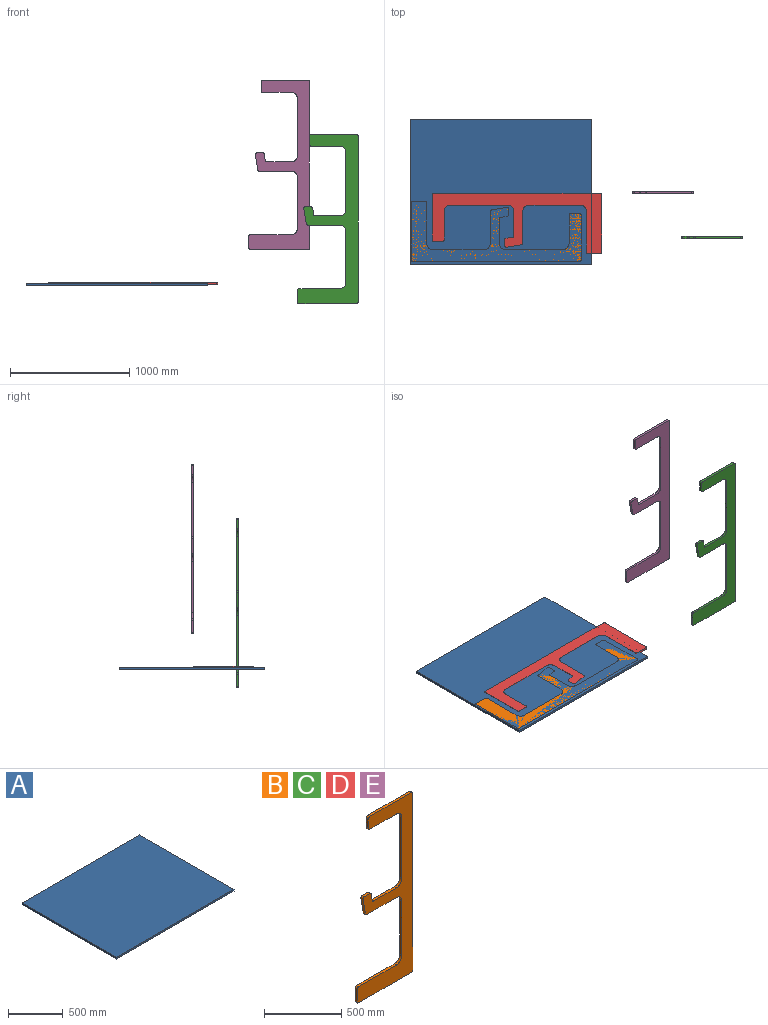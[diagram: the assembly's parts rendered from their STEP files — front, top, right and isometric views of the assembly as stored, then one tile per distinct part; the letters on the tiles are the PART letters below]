
ASSEMBLY  parts=5 mates=1
PART A: 6 faces, bbox 1524x1219.2x19.1 mm
  f0: plane 1524x19.05mm, normal (0,1,0), area 29032.2mm2, adj f1,f3,f4,f5
  f1: plane 1219.2x19.05mm, normal (-1,0,0), area 23225.8mm2, adj f0,f2,f4,f5
  f2: plane 1524x19.05mm, normal (0,-1,0), area 29032.2mm2, adj f1,f3,f4,f5
  f3: plane 1219.2x19.05mm, normal (1,0,0), area 23225.8mm2, adj f0,f2,f4,f5
  f4: plane 1524x1219.2mm, normal (0,0,1), area 1858060.8mm2, adj f0,f1,f2,f3
  f5: plane 1524x1219.2mm, normal (0,0,-1), area 1858060.8mm2, adj f0,f1,f2,f3
PART B: 30 faces, bbox 508x19.1x1422.4 mm
  f0: plane 54.98x19.05mm, normal (0.99,0,0.16), area 1061.7mm2, adj f1,f27,f28,f29
  f1: cylinder r=12.7mm len=19.05mm, axis (0,1,0), area 340.1mm2, adj f0,f2,f28,f29
  f2: plane 50.45x19.05mm, normal (0,0,1), area 961.1mm2, adj f1,f3,f28,f29
  f3: cylinder r=12.7mm len=19.05mm, axis (0,1,0), area 420mm2, adj f2,f4,f28,f29
  f4: plane 127x21.17mm, normal (-0.99,0,-0.16), area 2452.7mm2, adj f3,f5,f28,f29
  f5: cylinder r=12.7mm len=19.05mm, axis (0,1,0), area 340.1mm2, adj f4,f6,f28,f29
  f6: plane 268.64x19.05mm, normal (0,0,-1), area 5117.6mm2, adj f5,f7,f28,f29
  f7: cylinder r=50.8mm len=50.8mm, axis (0,1,0), area 1520.1mm2, adj f6,f8,f28,f29
  f8: plane 431.8x19.05mm, normal (-1,0,0), area 8225.8mm2, adj f7,f9,f28,f29
  f9: cylinder r=50.8mm len=50.8mm, axis (0,1,0), area 1520.1mm2, adj f8,f10,f28,f29
  f10: plane 342.9x19.05mm, normal (0,0,1), area 6532.2mm2, adj f9,f11,f28,f29
  f11: cylinder r=12.7mm len=19.05mm, axis (0,1,0), area 380mm2, adj f10,f12,f28,f29
  f12: plane 101.6x19.05mm, normal (-1,0,0), area 1935.5mm2, adj f11,f13,f28,f29
  f13: cylinder r=12.7mm len=19.05mm, axis (0,1,0), area 380mm2, adj f12,f14,f28,f29
  f14: plane 482.6x19.05mm, normal (0,0,-1), area 9193.5mm2, adj f13,f15,f28,f29
  f15: cylinder r=12.7mm len=19.05mm, axis (0,1,0), area 380mm2, adj f14,f16,f28,f29
  f16: plane 1397x19.05mm, normal (1,0,0), area 26612.8mm2, adj f15,f17,f28,f29
  f17: cylinder r=12.7mm len=19.05mm, axis (0,1,0), area 380mm2, adj f16,f18,f28,f29
  f18: plane 381x19.05mm, normal (0,0,1), area 7258.1mm2, adj f17,f19,f28,f29
  f19: cylinder r=12.7mm len=19.05mm, axis (0,1,0), area 380mm2, adj f18,f20,f28,f29
  f20: plane 76.2x19.05mm, normal (-1,0,0), area 1451.6mm2, adj f19,f21,f28,f29
  f21: cylinder r=12.7mm len=19.05mm, axis (0,1,0), area 380mm2, adj f20,f22,f28,f29
  f22: plane 241.3x19.05mm, normal (0,0,-1), area 4596.8mm2, adj f21,f23,f28,f29
  f23: cylinder r=50.8mm len=50.8mm, axis (0,1,0), area 1520.1mm2, adj f22,f24,f28,f29
  f24: plane 482.6x19.05mm, normal (-1,0,0), area 9193.5mm2, adj f23,f25,f28,f29
  f25: cylinder r=50.8mm len=50.8mm, axis (0,1,0), area 1520.1mm2, adj f24,f26,f28,f29
  f26: plane 205.14x19.05mm, normal (0,0,1), area 3907.9mm2, adj f25,f27,f28,f29
  f27: cylinder r=12.7mm len=19.05mm, axis (0,1,0), area 340.1mm2, adj f0,f26,f28,f29
  f28: plane 1422.4x508mm, normal (0,-1,0), area 260481.8mm2, adj f0,f1,f2,f3,f4,f5,f6,f7
  f29: plane 1422.4x508mm, normal (0,1,0), area 260481.8mm2, adj f0,f1,f2,f3,f4,f5,f6,f7
PART C: same geometry as B
PART D: same geometry as B
PART E: same geometry as B
PLACE A t=(762,609.6,-19.05)mm
PLACE B rot(axis=(-0.58,0.58,-0.58),120deg) t=(12.7,25.4,-9.53)mm
PLACE C t=(2784.03,228.25,-172.63)mm
PLACE D rot(axis=(-0.58,-0.58,0.58),120deg) t=(1607.08,600.29,-2.95)mm
PLACE E t=(2377.21,605.35,280.06)mm
MATE fastened A.f4 <-> B.f28  axis (0,0,1) through (0,0,0)mm
